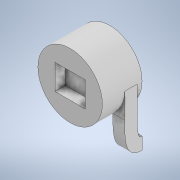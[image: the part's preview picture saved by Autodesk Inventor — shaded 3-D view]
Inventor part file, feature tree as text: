
AUTODESK INVENTOR PART (.ipt)
format: ipt  version: 2020 (Build 240168000, 168)  size: 147,968 bytes
history: native  units: in
note: dims shown in document units (in); Inventor stores cm internally (conversion verified against a paired STEP export)
features: sketch x5, projected_geometry x4, extrude x3, plane x2, sweep x1
ambient origin geometry x8: Origin, YZ Plane, XZ Plane, XY Plane, X Axis, Y Axis, Z Axis, Center Point
bodies: Solid1 (feature_tree)
feature tree (15):
  extrude  "Extrusion1"  Depth=3.1496in TaperAngle=0.0deg
  plane  "Work Plane1"
  plane  "Work Plane2"
  extrude  "Extrusion2"  Depth=0.9449in
  sweep  "Sweep1"
  extrude  "Extrusion3"  Depth=1.378in
  sketch  "Sketch1"  dims[d0=5.1181in d1=3.1496in d2=0.0in]
  sketch  "Sketch2"  dims[d3=-1.378in d4=0.9449in]
  projected_geometry  "Projected Loop1"
  sketch  "Sketch3"  dims[d5=0.9843in d6=0.0in d7=2.7559in]
  projected_geometry  "Projected Loop2"
  sketch  "Sketch4"  dims[d8=1.378in d9=1.378in]
  projected_geometry  "Projected Loop3"
  sketch  "Sketch5"  dims[d10=0.0in d11=0.0in d12=2.4in d13=2.0in d14=0.8135in d15=0.0in]
  projected_geometry  "Projected Loop4"
